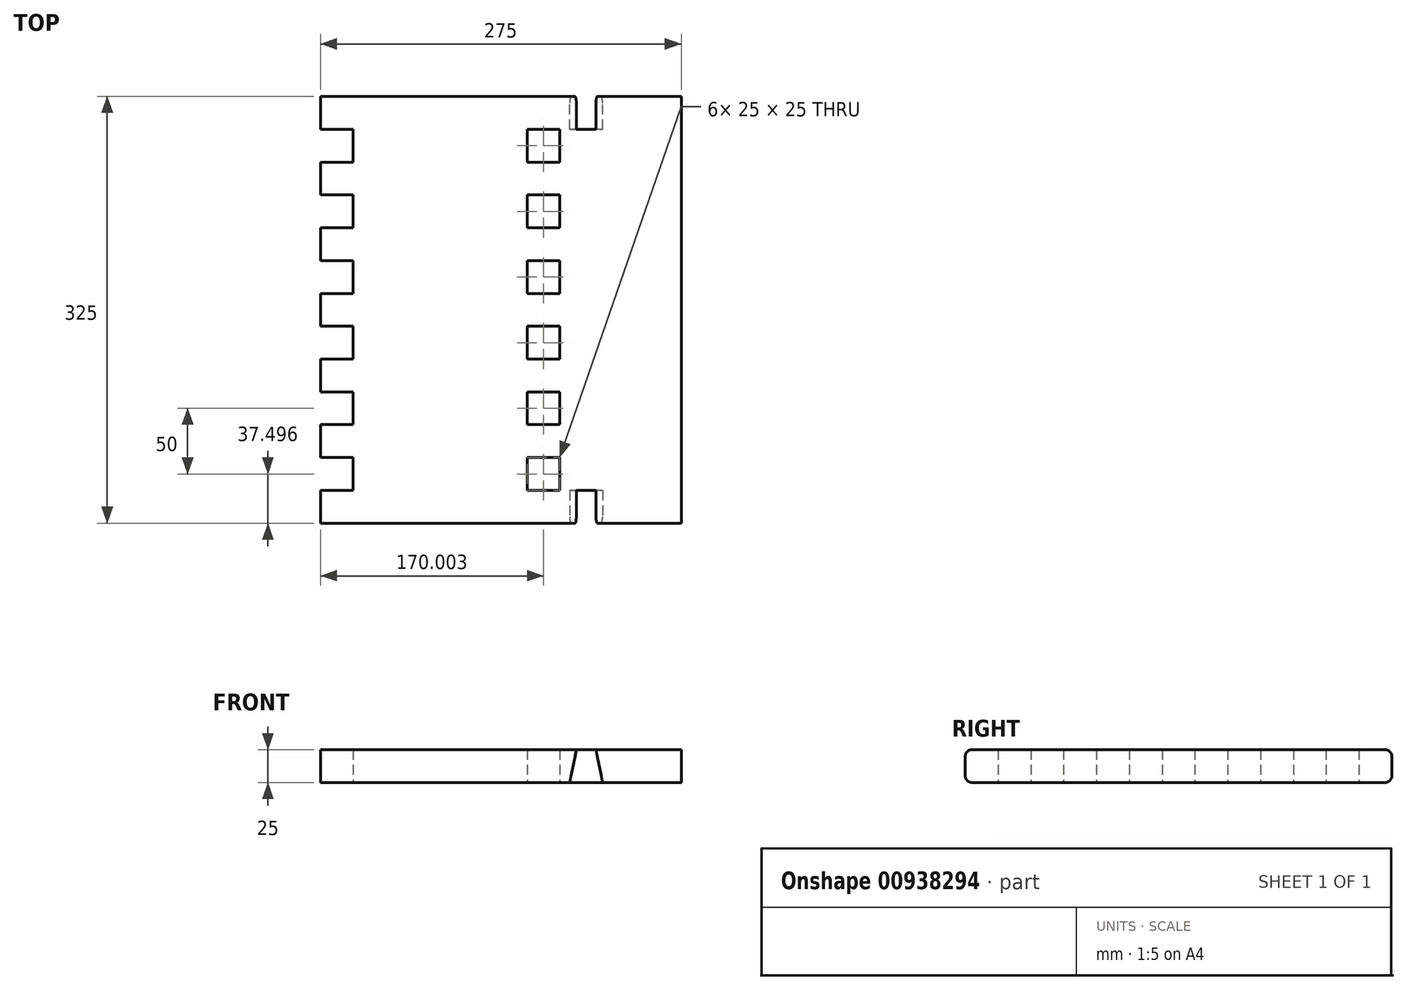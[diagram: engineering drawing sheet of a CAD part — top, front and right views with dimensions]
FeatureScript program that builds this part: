
annotation { "Feature Type Name" : "Feature", "Feature Type Description" : "" }
export const myFeature = defineFeature(function(context is Context, id is Id, definition is map)
    precondition{}
    {
        {
            var Q0;
            Q0=qCreatedBy(makeId("Top.planeOp"),FACE);
            var sketch = newSketch(context, id + "F0", { "sketchPlane" : qUnion([Q0])});
            skLineSegment(sketch, "E0.bottom", {"start": v(38.86, -141.93) * mm, "end": v(288.86, -141.93) * mm});
            skLineSegment(sketch, "E0.top", {"start": v(38.86, 183.07) * mm, "end": v(288.86, 183.07) * mm});
            skLineSegment(sketch, "E0.left", {"start": v(38.86, -141.93) * mm, "end": v(38.86, 183.07) * mm});
            skLineSegment(sketch, "E0.right", {"start": v(288.86, -141.93) * mm, "end": v(288.86, 183.07) * mm});
            skLineSegment(sketch, "E1.bottom", {"start": v(38.86, -141.93) * mm, "end": v(13.86, -141.93) * mm});
            skLineSegment(sketch, "E1.top", {"start": v(38.86, -116.93) * mm, "end": v(13.86, -116.93) * mm});
            skLineSegment(sketch, "E1.left", {"start": v(38.86, -141.93) * mm, "end": v(38.86, -116.93) * mm});
            skLineSegment(sketch, "E1.right", {"start": v(13.86, -141.93) * mm, "end": v(13.86, -116.93) * mm});
            skLineSegment(sketch, "E2.bottom", {"start": v(38.86, -91.93) * mm, "end": v(13.86, -91.93) * mm});
            skLineSegment(sketch, "E2.top", {"start": v(38.86, -66.93) * mm, "end": v(13.86, -66.93) * mm});
            skLineSegment(sketch, "E2.left", {"start": v(38.86, -91.93) * mm, "end": v(38.86, -66.93) * mm});
            skLineSegment(sketch, "E2.right", {"start": v(13.86, -91.93) * mm, "end": v(13.86, -66.93) * mm});
            skLineSegment(sketch, "E3.bottom", {"start": v(38.86, -41.93) * mm, "end": v(13.86, -41.93) * mm});
            skLineSegment(sketch, "E3.top", {"start": v(38.86, -16.93) * mm, "end": v(13.86, -16.93) * mm});
            skLineSegment(sketch, "E3.left", {"start": v(38.86, -41.93) * mm, "end": v(38.86, -16.93) * mm});
            skLineSegment(sketch, "E3.right", {"start": v(13.86, -41.93) * mm, "end": v(13.86, -16.93) * mm});
            skLineSegment(sketch, "E4.bottom", {"start": v(38.86, 58.07) * mm, "end": v(13.86, 58.07) * mm});
            skLineSegment(sketch, "E4.top", {"start": v(38.86, 83.07) * mm, "end": v(13.86, 83.07) * mm});
            skLineSegment(sketch, "E4.left", {"start": v(38.86, 58.07) * mm, "end": v(38.86, 83.07) * mm});
            skLineSegment(sketch, "E4.right", {"start": v(13.86, 58.07) * mm, "end": v(13.86, 83.07) * mm});
            skLineSegment(sketch, "E5.bottom", {"start": v(38.86, 108.07) * mm, "end": v(13.86, 108.07) * mm});
            skLineSegment(sketch, "E5.top", {"start": v(38.86, 133.07) * mm, "end": v(13.86, 133.07) * mm});
            skLineSegment(sketch, "E5.left", {"start": v(38.86, 108.07) * mm, "end": v(38.86, 133.07) * mm});
            skLineSegment(sketch, "E5.right", {"start": v(13.86, 108.07) * mm, "end": v(13.86, 133.07) * mm});
            skLineSegment(sketch, "E6.bottom", {"start": v(38.86, 8.07) * mm, "end": v(13.86, 8.07) * mm});
            skLineSegment(sketch, "E6.top", {"start": v(38.86, 33.07) * mm, "end": v(13.86, 33.07) * mm});
            skLineSegment(sketch, "E6.left", {"start": v(38.86, 8.07) * mm, "end": v(38.86, 33.07) * mm});
            skLineSegment(sketch, "E6.right", {"start": v(13.86, 8.07) * mm, "end": v(13.86, 33.07) * mm});
            skLineSegment(sketch, "E7.bottom", {"start": v(38.86, 183.07) * mm, "end": v(13.86, 183.07) * mm});
            skLineSegment(sketch, "E7.top", {"start": v(38.86, 158.07) * mm, "end": v(13.86, 158.07) * mm});
            skLineSegment(sketch, "E7.left", {"start": v(38.86, 183.07) * mm, "end": v(38.86, 158.07) * mm});
            skLineSegment(sketch, "E7.right", {"start": v(13.86, 183.07) * mm, "end": v(13.86, 158.07) * mm});
            skSolve(sketch);
        }
        {
            var Q0;
            {var subQ10=sQuery(id+"F0.wireOp",EDGE,"E0.bottom");Q0=makeQuery(id+"F0.imprint","IMPRINT",FACE,{"disambiguationData":[TD([[makeQuery(id+"F0.imprint","IMPRINT",EDGE,{"derivedFrom":subQ10}),1.0]])]});}
            var Q1;
            {var subQ0=sQuery(id+"F0.wireOp",EDGE,"E1.bottom");Q1=makeQuery(id+"F0.imprint","IMPRINT",FACE,{"disambiguationData":[TD([[makeQuery(id+"F0.imprint","IMPRINT",EDGE,{"derivedFrom":subQ0}),-1.0]])]});}
            var Q2;
            {var subQ0=sQuery(id+"F0.wireOp",EDGE,"E2.bottom");Q2=makeQuery(id+"F0.imprint","IMPRINT",FACE,{"disambiguationData":[TD([[makeQuery(id+"F0.imprint","IMPRINT",EDGE,{"derivedFrom":subQ0}),-1.0]])]});}
            var Q3;
            {var subQ0=sQuery(id+"F0.wireOp",EDGE,"E3.bottom");Q3=makeQuery(id+"F0.imprint","IMPRINT",FACE,{"disambiguationData":[TD([[makeQuery(id+"F0.imprint","IMPRINT",EDGE,{"derivedFrom":subQ0}),-1.0]])]});}
            var Q4;
            {var subQ0=sQuery(id+"F0.wireOp",EDGE,"E6.bottom");Q4=makeQuery(id+"F0.imprint","IMPRINT",FACE,{"disambiguationData":[TD([[makeQuery(id+"F0.imprint","IMPRINT",EDGE,{"derivedFrom":subQ0}),-1.0]])]});}
            var Q5;
            {var subQ0=sQuery(id+"F0.wireOp",EDGE,"E4.bottom");Q5=makeQuery(id+"F0.imprint","IMPRINT",FACE,{"disambiguationData":[TD([[makeQuery(id+"F0.imprint","IMPRINT",EDGE,{"derivedFrom":subQ0}),-1.0]])]});}
            var Q6;
            {var subQ2=sQuery(id+"F0.wireOp",EDGE,"E5.bottom");Q6=makeQuery(id+"F0.imprint","IMPRINT",FACE,{"disambiguationData":[TD([[makeQuery(id+"F0.imprint","IMPRINT",EDGE,{"derivedFrom":subQ2}),-1.0]])]});}
            var Q7;
            {var subQ0=sQuery(id+"F0.wireOp",EDGE,"E7.bottom");Q7=makeQuery(id+"F0.imprint","IMPRINT",FACE,{"disambiguationData":[TD([[makeQuery(id+"F0.imprint","IMPRINT",EDGE,{"derivedFrom":subQ0}),1.0]])]});}
            extrude(context, id + "F1", {"entities" : qUnion([Q0, Q1, Q2, Q3, Q4, Q5, Q6, Q7]), "depth" : 25 * mm, "offsetDistance" : 25 * mm});
        }
        {
            var Q0;
            Q0=makeQuery(id+"F1.opExtrude","SWEPT_FACE",FACE,{"disambiguationData":[OSD([sQuery(id+"F0.wireOp",EDGE,"E0.bottom"),sQuery(id+"F0.wireOp",EDGE,"E1.bottom")])]});
            var sketch = newSketch(context, id + "F2", { "sketchPlane" : qUnion([Q0])});
            skLineSegment(sketch, "E8", {"start": v(203.86, 0) * mm, "end": v(228.86, 0) * mm});
            skLineSegment(sketch, "E9", {"start": v(228.86, 0) * mm, "end": v(223.86, 25) * mm});
            skLineSegment(sketch, "E10", {"start": v(223.86, 25) * mm, "end": v(208.86, 25) * mm});
            skLineSegment(sketch, "E11", {"start": v(208.86, 25) * mm, "end": v(203.86, 0) * mm});
            skSolve(sketch);
        }
        {
            var Q0;
            Q0=makeQuery(id+"F2.imprint","IMPRINT",FACE,{"disambiguationData":[TD([[makeQuery(id+"F2.imprint","IMPRINT",EDGE,{"derivedFrom":sQuery(id+"F2.wireOp",EDGE,"E8")}),1.0]])]});
            extrude(context, id + "F3", {"entities" : qUnion([Q0]), "operationType" : NewBodyOperationType.REMOVE, "oppositeDirection" : true, "depth" : 25 * mm, "offsetDistance" : 25 * mm});
        }
        {
            var Q0;
            Q0=makeQuery(id+"F1.opExtrude","CAP_EDGE",EDGE,{"disambiguationData":[OSD([sQuery(id+"F0.wireOp",EDGE,"E0.right")])],"isStart":true});
            cPoint(context, id + "F4", {"entities" : qUnion([Q0]), "parameter" : 0.5});
        }
        {
            var Q0;
            Q0=makeQuery(id+"F1.opExtrude","CAP_EDGE",EDGE,{"disambiguationData":[OSD([sQuery(id+"F0.wireOp",EDGE,"E0.right")])],"isStart":false});
            cPoint(context, id + "F5", {"entities" : qUnion([Q0]), "parameter" : 0.5});
        }
        {
            var Q0;
            Q0=makeQuery(id+"F1.opExtrude","CAP_EDGE",EDGE,{"disambiguationData":[OSD([sQuery(id+"F0.wireOp",EDGE,"E6.right")])],"isStart":false});
            cPoint(context, id + "F6", {"entities" : qUnion([Q0]), "parameter" : 0.5});
        }
        {
            var Q0;
            Q0 = qCreatedBy(id + "F4" ,VERTEX);
            var Q1;
            Q1 = qCreatedBy(id + "F5" ,VERTEX);
            var Q2;
            Q2 = qCreatedBy(id + "F6" ,VERTEX);
            cPlane(context, id + "F7", {"entities" : qUnion([Q0, Q1, Q2]), "cplaneType" : CPlaneType.THREE_POINT, "offset" : 25 * mm, "width" : 150 * mm, "height" : 150 * mm});
        }
        {
            var Q0;
            Q0=makeQuery(id+"F1.opExtrude","SWEPT_BODY",BODY,{"disambiguationData":[OSD([sQuery(id+"F0.wireOp",EDGE,"E0.bottom"),sQuery(id+"F0.wireOp",EDGE,"E0.top"),sQuery(id+"F0.wireOp",EDGE,"E0.left"),sQuery(id+"F0.wireOp",EDGE,"E0.right"),sQuery(id+"F0.wireOp",EDGE,"E1.bottom"),sQuery(id+"F0.wireOp",EDGE,"E1.top"),sQuery(id+"F0.wireOp",EDGE,"E1.right"),sQuery(id+"F0.wireOp",EDGE,"E2.bottom"),sQuery(id+"F0.wireOp",EDGE,"E2.top"),sQuery(id+"F0.wireOp",EDGE,"E2.right"),sQuery(id+"F0.wireOp",EDGE,"E3.bottom"),sQuery(id+"F0.wireOp",EDGE,"E3.top"),sQuery(id+"F0.wireOp",EDGE,"E3.right"),sQuery(id+"F0.wireOp",EDGE,"E4.bottom"),sQuery(id+"F0.wireOp",EDGE,"E4.top"),sQuery(id+"F0.wireOp",EDGE,"E4.right"),sQuery(id+"F0.wireOp",EDGE,"E5.bottom"),sQuery(id+"F0.wireOp",EDGE,"E5.top"),sQuery(id+"F0.wireOp",EDGE,"E5.right"),sQuery(id+"F0.wireOp",EDGE,"E6.bottom"),sQuery(id+"F0.wireOp",EDGE,"E6.top"),sQuery(id+"F0.wireOp",EDGE,"E6.right"),sQuery(id+"F0.wireOp",EDGE,"E7.bottom"),sQuery(id+"F0.wireOp",EDGE,"E7.top"),sQuery(id+"F0.wireOp",EDGE,"E7.right")])]});
            var Q1;
            Q1=qCreatedBy(id+"F7.planeOp",FACE);
            mirror(context, id + "F8", {"operationType" : NewBodyOperationType.INTERSECT, "entities" : qUnion([Q0]), "mirrorPlane" : qUnion([Q1])});
        }
        {
            var Q0;
            Q0=makeQuery(id+"F1.opExtrude","CAP_FACE",FACE,{"disambiguationData":[OSD([sQuery(id+"F0.wireOp",EDGE,"E0.bottom"),sQuery(id+"F0.wireOp",EDGE,"E0.top"),sQuery(id+"F0.wireOp",EDGE,"E0.left"),sQuery(id+"F0.wireOp",EDGE,"E0.right"),sQuery(id+"F0.wireOp",EDGE,"E1.bottom"),sQuery(id+"F0.wireOp",EDGE,"E1.top"),sQuery(id+"F0.wireOp",EDGE,"E1.right"),sQuery(id+"F0.wireOp",EDGE,"E2.bottom"),sQuery(id+"F0.wireOp",EDGE,"E2.top"),sQuery(id+"F0.wireOp",EDGE,"E2.right"),sQuery(id+"F0.wireOp",EDGE,"E3.bottom"),sQuery(id+"F0.wireOp",EDGE,"E3.top"),sQuery(id+"F0.wireOp",EDGE,"E3.right"),sQuery(id+"F0.wireOp",EDGE,"E4.bottom"),sQuery(id+"F0.wireOp",EDGE,"E4.top"),sQuery(id+"F0.wireOp",EDGE,"E4.right"),sQuery(id+"F0.wireOp",EDGE,"E5.bottom"),sQuery(id+"F0.wireOp",EDGE,"E5.top"),sQuery(id+"F0.wireOp",EDGE,"E5.right"),sQuery(id+"F0.wireOp",EDGE,"E6.bottom"),sQuery(id+"F0.wireOp",EDGE,"E6.top"),sQuery(id+"F0.wireOp",EDGE,"E6.right"),sQuery(id+"F0.wireOp",EDGE,"E7.bottom"),sQuery(id+"F0.wireOp",EDGE,"E7.top"),sQuery(id+"F0.wireOp",EDGE,"E7.right")])],"isStart":true});
            var sketch = newSketch(context, id + "F9", { "sketchPlane" : qUnion([Q0])});
            skLineSegment(sketch, "E12.bottom", {"start": v(171.36, -158.07) * mm, "end": v(196.36, -158.07) * mm});
            skLineSegment(sketch, "E12.top", {"start": v(171.36, -133.07) * mm, "end": v(196.36, -133.07) * mm});
            skLineSegment(sketch, "E12.left", {"start": v(171.36, -158.07) * mm, "end": v(171.36, -133.07) * mm});
            skLineSegment(sketch, "E12.right", {"start": v(196.36, -158.07) * mm, "end": v(196.36, -133.07) * mm});
            skLineSegment(sketch, "E13.bottom", {"start": v(171.36, -108.07) * mm, "end": v(196.36, -108.07) * mm});
            skLineSegment(sketch, "E13.top", {"start": v(171.36, -83.07) * mm, "end": v(196.36, -83.07) * mm});
            skLineSegment(sketch, "E13.left", {"start": v(171.36, -108.07) * mm, "end": v(171.36, -83.07) * mm});
            skLineSegment(sketch, "E13.right", {"start": v(196.36, -108.07) * mm, "end": v(196.36, -83.07) * mm});
            skLineSegment(sketch, "E14.bottom", {"start": v(171.36, -58.07) * mm, "end": v(196.36, -58.07) * mm});
            skLineSegment(sketch, "E14.top", {"start": v(171.36, -33.07) * mm, "end": v(196.36, -33.07) * mm});
            skLineSegment(sketch, "E14.left", {"start": v(171.36, -58.07) * mm, "end": v(171.36, -33.07) * mm});
            skLineSegment(sketch, "E14.right", {"start": v(196.36, -58.07) * mm, "end": v(196.36, -33.07) * mm});
            skLineSegment(sketch, "E15.bottom", {"start": v(171.36, -8.07) * mm, "end": v(196.36, -8.07) * mm});
            skLineSegment(sketch, "E15.top", {"start": v(171.36, 16.93) * mm, "end": v(196.36, 16.93) * mm});
            skLineSegment(sketch, "E15.left", {"start": v(171.36, -8.07) * mm, "end": v(171.36, 16.93) * mm});
            skLineSegment(sketch, "E15.right", {"start": v(196.36, -8.07) * mm, "end": v(196.36, 16.93) * mm});
            skLineSegment(sketch, "E16.bottom", {"start": v(171.36, 41.93) * mm, "end": v(196.36, 41.93) * mm});
            skLineSegment(sketch, "E16.top", {"start": v(171.36, 66.93) * mm, "end": v(196.36, 66.93) * mm});
            skLineSegment(sketch, "E16.left", {"start": v(171.36, 41.93) * mm, "end": v(171.36, 66.93) * mm});
            skLineSegment(sketch, "E16.right", {"start": v(196.36, 41.93) * mm, "end": v(196.36, 66.93) * mm});
            skLineSegment(sketch, "E17.bottom", {"start": v(148.09, 516.7) * mm, "end": v(173.09, 516.7) * mm});
            skLineSegment(sketch, "E17.top", {"start": v(148.09, 541.7) * mm, "end": v(173.09, 541.7) * mm});
            skLineSegment(sketch, "E17.left", {"start": v(148.09, 516.7) * mm, "end": v(148.09, 541.7) * mm});
            skLineSegment(sketch, "E17.right", {"start": v(173.09, 516.7) * mm, "end": v(173.09, 541.7) * mm});
            skLineSegment(sketch, "E18.bottom", {"start": v(171.36, 91.93) * mm, "end": v(196.36, 91.93) * mm});
            skLineSegment(sketch, "E18.top", {"start": v(171.36, 116.93) * mm, "end": v(196.36, 116.93) * mm});
            skLineSegment(sketch, "E18.left", {"start": v(171.36, 91.93) * mm, "end": v(171.36, 116.93) * mm});
            skLineSegment(sketch, "E18.right", {"start": v(196.36, 91.93) * mm, "end": v(196.36, 116.93) * mm});
            skSolve(sketch);
        }
        {
            var Q0;
            Q0=makeQuery(id+"F9.imprint","IMPRINT",FACE,{"disambiguationData":[TD([[makeQuery(id+"F9.imprint","IMPRINT",EDGE,{"derivedFrom":sQuery(id+"F9.wireOp",EDGE,"E12.bottom")}),1.0]])]});
            var Q1;
            Q1=makeQuery(id+"F9.imprint","IMPRINT",FACE,{"disambiguationData":[TD([[makeQuery(id+"F9.imprint","IMPRINT",EDGE,{"derivedFrom":sQuery(id+"F9.wireOp",EDGE,"E13.bottom")}),1.0]])]});
            var Q2;
            Q2=makeQuery(id+"F9.imprint","IMPRINT",FACE,{"disambiguationData":[TD([[makeQuery(id+"F9.imprint","IMPRINT",EDGE,{"derivedFrom":sQuery(id+"F9.wireOp",EDGE,"E14.bottom")}),1.0]])]});
            var Q3;
            Q3=makeQuery(id+"F9.imprint","IMPRINT",FACE,{"disambiguationData":[TD([[makeQuery(id+"F9.imprint","IMPRINT",EDGE,{"derivedFrom":sQuery(id+"F9.wireOp",EDGE,"E15.bottom")}),1.0]])]});
            var Q4;
            Q4=makeQuery(id+"F9.imprint","IMPRINT",FACE,{"disambiguationData":[TD([[makeQuery(id+"F9.imprint","IMPRINT",EDGE,{"derivedFrom":sQuery(id+"F9.wireOp",EDGE,"E16.bottom")}),1.0]])]});
            var Q5;
            Q5=makeQuery(id+"F9.imprint","IMPRINT",FACE,{"disambiguationData":[TD([[makeQuery(id+"F9.imprint","IMPRINT",EDGE,{"derivedFrom":sQuery(id+"F9.wireOp",EDGE,"E18.bottom")}),1.0]])]});
            extrude(context, id + "F10", {"entities" : qUnion([Q0, Q1, Q2, Q3, Q4, Q5]), "operationType" : NewBodyOperationType.REMOVE, "oppositeDirection" : true, "depth" : 25 * mm, "offsetDistance" : 25 * mm});
        }
        {
            var Q0;
            {var subQ0=sQuery(id+"F0.wireOp",EDGE,"E1.right");var subQ1=sQuery(id+"F0.wireOp",EDGE,"E1.bottom");var subQ2=sQuery(id+"F0.wireOp",EDGE,"E0.bottom");Q0=makeQuery(id+"F3.boolean.opBoolean","SPLIT",EDGE,{"disambiguationData":[TD([makeQuery(id+"F1.opExtrude","SWEPT_FACE",FACE,{"disambiguationData":[OSD([subQ0])]})])],"derivedFrom":makeQuery(id+"F1.opExtrude","CAP_EDGE",EDGE,{"disambiguationData":[OSD([subQ2,subQ1])],"isStart":true})});}
            var Q1;
            {var subQ0=sQuery(id+"F0.wireOp",EDGE,"E1.right");var subQ1=sQuery(id+"F0.wireOp",EDGE,"E1.bottom");var subQ2=sQuery(id+"F0.wireOp",EDGE,"E0.bottom");Q1=makeQuery(id+"F3.boolean.opBoolean","SPLIT",EDGE,{"disambiguationData":[TD([makeQuery(id+"F1.opExtrude","SWEPT_FACE",FACE,{"disambiguationData":[OSD([subQ0])]})])],"derivedFrom":makeQuery(id+"F1.opExtrude","CAP_EDGE",EDGE,{"disambiguationData":[OSD([subQ2,subQ1])],"isStart":false})});}
            var Q2;
            {var subQ0=sQuery(id+"F0.wireOp",EDGE,"E1.bottom");var subQ1=sQuery(id+"F0.wireOp",EDGE,"E0.right");var subQ2=sQuery(id+"F0.wireOp",EDGE,"E0.bottom");Q2=makeQuery(id+"F3.boolean.opBoolean","SPLIT",EDGE,{"disambiguationData":[TD([makeQuery(id+"F1.opExtrude","SWEPT_FACE",FACE,{"disambiguationData":[OSD([subQ1])]})])],"derivedFrom":makeQuery(id+"F1.opExtrude","CAP_EDGE",EDGE,{"disambiguationData":[OSD([subQ2,subQ0])],"isStart":false})});}
            var Q3;
            {var subQ0=sQuery(id+"F0.wireOp",EDGE,"E1.bottom");var subQ1=sQuery(id+"F0.wireOp",EDGE,"E0.right");var subQ2=sQuery(id+"F0.wireOp",EDGE,"E0.bottom");Q3=makeQuery(id+"F3.boolean.opBoolean","SPLIT",EDGE,{"disambiguationData":[TD([makeQuery(id+"F1.opExtrude","SWEPT_FACE",FACE,{"disambiguationData":[OSD([subQ1])]})])],"derivedFrom":makeQuery(id+"F1.opExtrude","CAP_EDGE",EDGE,{"disambiguationData":[OSD([subQ2,subQ0])],"isStart":true})});}
            fillet(context, id + "F11", {"entities" : qUnion([Q0, Q1, Q2, Q3]), "radius" : 5 * mm, "tangentPropagation" : true, "allowEdgeOverflow" : false});
        }
        {
            var Q0;
            {var subQ0=sQuery(id+"F0.wireOp",EDGE,"E7.right");var subQ1=sQuery(id+"F0.wireOp",EDGE,"E7.bottom");var subQ2=sQuery(id+"F0.wireOp",EDGE,"E0.top");Q0=makeQuery(id+"F8.boolean.opBoolean","SPLIT",EDGE,{"disambiguationData":[TD([makeQuery(id+"F1.opExtrude","SWEPT_FACE",FACE,{"disambiguationData":[OSD([subQ0])]})])],"derivedFrom":makeQuery(id+"F1.opExtrude","CAP_EDGE",EDGE,{"disambiguationData":[OSD([subQ2,subQ1])],"isStart":false})});}
            var Q1;
            {var subQ0=sQuery(id+"F0.wireOp",EDGE,"E7.right");var subQ1=sQuery(id+"F0.wireOp",EDGE,"E7.bottom");var subQ2=sQuery(id+"F0.wireOp",EDGE,"E0.top");Q1=makeQuery(id+"F8.boolean.opBoolean","SPLIT",EDGE,{"disambiguationData":[TD([makeQuery(id+"F1.opExtrude","SWEPT_FACE",FACE,{"disambiguationData":[OSD([subQ0])]})])],"derivedFrom":makeQuery(id+"F1.opExtrude","CAP_EDGE",EDGE,{"disambiguationData":[OSD([subQ2,subQ1])],"isStart":true})});}
            var Q2;
            {var subQ0=sQuery(id+"F0.wireOp",EDGE,"E7.bottom");var subQ1=sQuery(id+"F0.wireOp",EDGE,"E0.right");var subQ2=sQuery(id+"F0.wireOp",EDGE,"E0.top");Q2=makeQuery(id+"F8.boolean.opBoolean","SPLIT",EDGE,{"disambiguationData":[TD([makeQuery(id+"F1.opExtrude","SWEPT_FACE",FACE,{"disambiguationData":[OSD([subQ1])]})])],"derivedFrom":makeQuery(id+"F1.opExtrude","CAP_EDGE",EDGE,{"disambiguationData":[OSD([subQ2,subQ0])],"isStart":true})});}
            var Q3;
            {var subQ0=sQuery(id+"F0.wireOp",EDGE,"E7.bottom");var subQ1=sQuery(id+"F0.wireOp",EDGE,"E0.right");var subQ2=sQuery(id+"F0.wireOp",EDGE,"E0.top");Q3=makeQuery(id+"F8.boolean.opBoolean","SPLIT",EDGE,{"disambiguationData":[TD([makeQuery(id+"F1.opExtrude","SWEPT_FACE",FACE,{"disambiguationData":[OSD([subQ1])]})])],"derivedFrom":makeQuery(id+"F1.opExtrude","CAP_EDGE",EDGE,{"disambiguationData":[OSD([subQ2,subQ0])],"isStart":false})});}
            fillet(context, id + "F12", {"entities" : qUnion([Q0, Q1, Q2, Q3]), "radius" : 5 * mm, "tangentPropagation" : true, "allowEdgeOverflow" : false});
        }
    });
